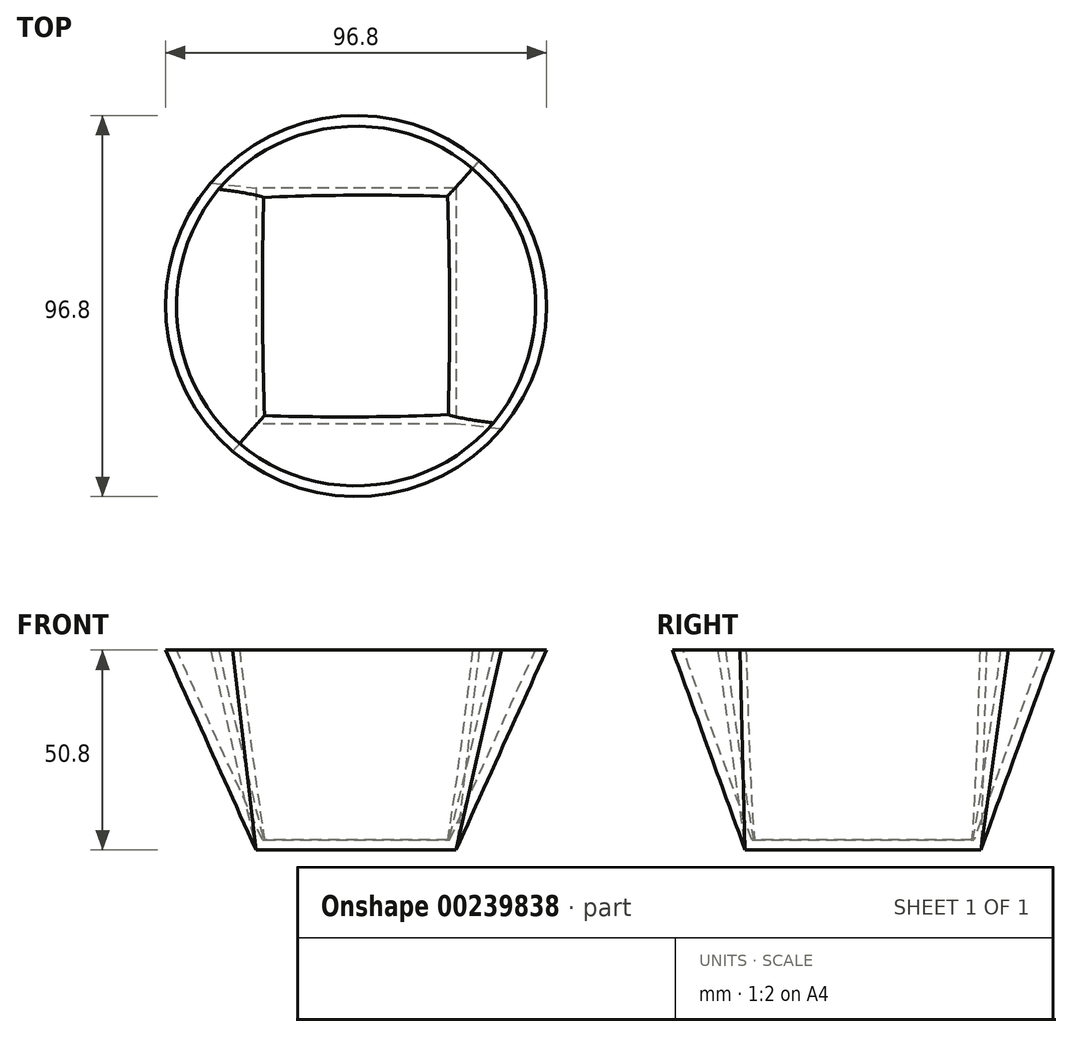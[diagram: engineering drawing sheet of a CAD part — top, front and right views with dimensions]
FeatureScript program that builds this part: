
annotation { "Feature Type Name" : "Feature", "Feature Type Description" : "" }
export const myFeature = defineFeature(function(context is Context, id is Id, definition is map)
    precondition{}
    {
        {
            var Q0;
            Q0=qCreatedBy(makeId("Top.planeOp"),FACE);
            var sketch = newSketch(context, id + "F0", { "sketchPlane" : qUnion([Q0])});
            skLineSegment(sketch, "E0.bottom", {"start": v(25.4, 29.95) * mm, "end": v(-25.4, 29.95) * mm});
            skLineSegment(sketch, "E0.top", {"start": v(25.4, -29.95) * mm, "end": v(-25.4, -29.95) * mm});
            skLineSegment(sketch, "E0.left", {"start": v(25.4, 29.95) * mm, "end": v(25.4, -29.95) * mm});
            skLineSegment(sketch, "E0.right", {"start": v(-25.4, 29.95) * mm, "end": v(-25.4, -29.95) * mm});
            skPoint(sketch, "E0.middle", {"position": v(0, 0) * mm});
            skSolve(sketch);
        }
        {
            var Q0;
            Q0=qCreatedBy(makeId("Top.planeOp"),FACE);
            cPlane(context, id + "F1", {"entities" : qUnion([Q0]), "cplaneType" : CPlaneType.OFFSET, "offset" : 50.8 * mm, "width" : 152.4 * mm, "height" : 152.4 * mm});
        }
        {
            var Q0;
            Q0=qCreatedBy(id+"F1.planeOp",FACE);
            var sketch = newSketch(context, id + "F2", { "sketchPlane" : qUnion([Q0])});
            skCircle(sketch, "E1", {"center": v(0, 0) * mm, "radius": 48.4 * mm});
            skSolve(sketch);
        }
        {
            var Q0;
            Q0=makeQuery(id+"F2.imprint","IMPRINT",FACE,{"disambiguationData":[TD([[makeQuery(id+"F2.imprint","IMPRINT",EDGE,{"derivedFrom":sQuery(id+"F2.wireOp",EDGE,"E1")}),1.0]])]});
            var Q1;
            Q1=makeQuery(id+"F0.imprint","IMPRINT",FACE,{"disambiguationData":[TD([[makeQuery(id+"F0.imprint","IMPRINT",EDGE,{"derivedFrom":sQuery(id+"F0.wireOp",EDGE,"E0.bottom")}),1.0]])]});
            loft(context, id + "F3", {"sheetProfilesArray" : [{ "sheetProfileEntities" : qUnion([Q0]) }, { "sheetProfileEntities" : qUnion([Q1]) }]});
        }
        {
            var Q0;
            Q0=makeQuery(id+"F3.opLoft","CAP_FACE",FACE,{"disambiguationData":[OSD([makeQuery(id+"F2.imprint","IMPRINT",FACE,{"disambiguationData":[TD([[makeQuery(id+"F2.imprint","IMPRINT",EDGE,{"derivedFrom":sQuery(id+"F2.wireOp",EDGE,"E1")}),1.0]])]})])],"isStart":true});
            shell(context, id + "F4", {"entities" : qUnion([Q0]), "thickness" : 2.54 * mm});
        }
    });
